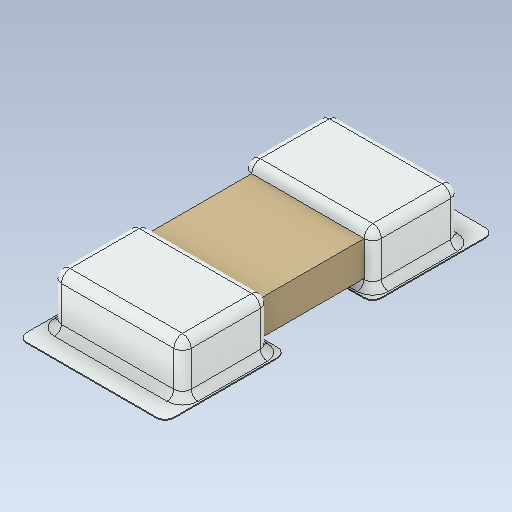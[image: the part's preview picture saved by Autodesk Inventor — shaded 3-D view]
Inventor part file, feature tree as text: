
AUTODESK INVENTOR PART (.ipt)
format: ipt  version: 2020.1 (Build 241239000, 239)  size: 173,056 bytes
history: native  units: mm
features: fillet x1
ambient origin geometry x8: Origin, YZ Plane, XZ Plane, XY Plane, X Axis, Y Axis, Z Axis, Center Point
bodies: Solid1 (feature_tree)
feature tree (1):
  fillet  "Fillet2"  [1 undecoded]
note: 1 required parameter value undecoded (feature->parameter linkage not recoverable at this tier; creation-order binding heuristic only, values carry confidence <= 0.55)
